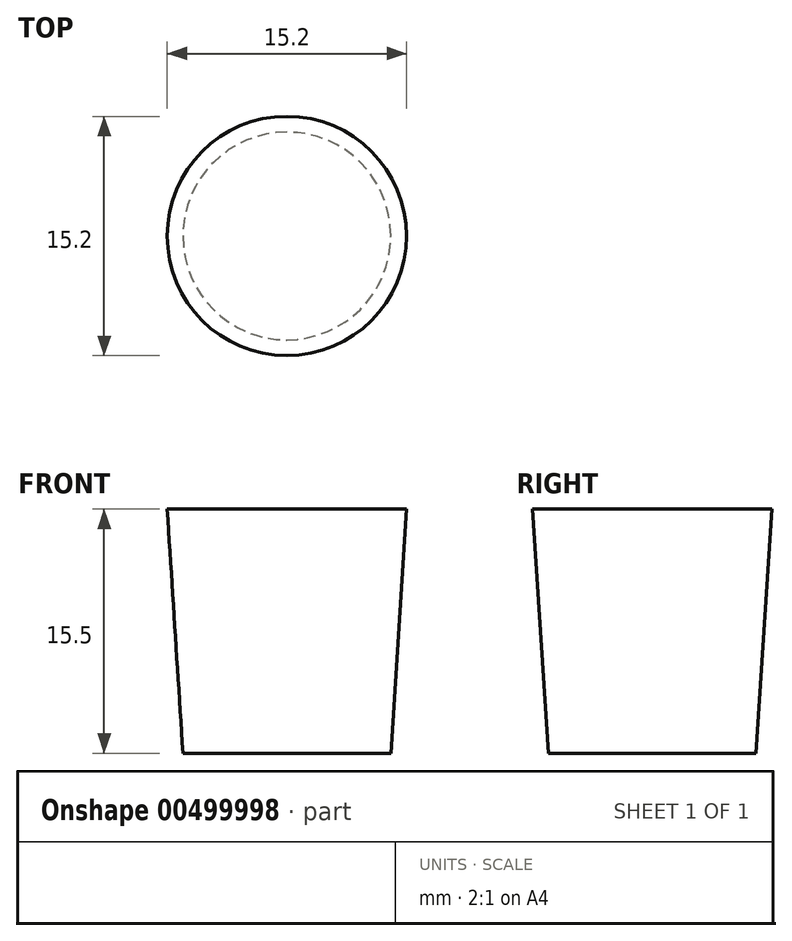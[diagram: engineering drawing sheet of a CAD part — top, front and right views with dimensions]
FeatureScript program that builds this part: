
annotation { "Feature Type Name" : "Feature", "Feature Type Description" : "" }
export const myFeature = defineFeature(function(context is Context, id is Id, definition is map)
    precondition{}
    {
        {
            var Q0;
            Q0=qCreatedBy(makeId("Front.planeOp"),FACE);
            var sketch = newSketch(context, id + "F0", { "sketchPlane" : qUnion([Q0])});
            skLineSegment(sketch, "E0", {"start": v(0, 12.08) * mm, "end": v(-7.6, 12.08) * mm});
            skLineSegment(sketch, "E1", {"start": v(-7.6, 12.08) * mm, "end": v(-6.6, -3.42) * mm});
            skLineSegment(sketch, "E2", {"start": v(-6.6, -3.42) * mm, "end": v(0, -3.42) * mm});
            skLineSegment(sketch, "E3", {"start": v(0, -3.42) * mm, "end": v(0, 12.08) * mm});
            skSolve(sketch);
        }
        {
            var Q0;
            Q0=makeQuery(id+"F0.imprint","IMPRINT",FACE,{"disambiguationData":[TD([[makeQuery(id+"F0.imprint","IMPRINT",EDGE,{"derivedFrom":sQuery(id+"F0.wireOp",EDGE,"E0")}),1.0]])]});
            var Q1;
            Q1=sQuery(id+"F0.wireOp",EDGE,"E3");
            revolve(context, id + "F1", {"entities" : qUnion([Q0]), "axis" : qUnion([Q1]), "revolveType" : RevolveType.FULL});
        }
    });
